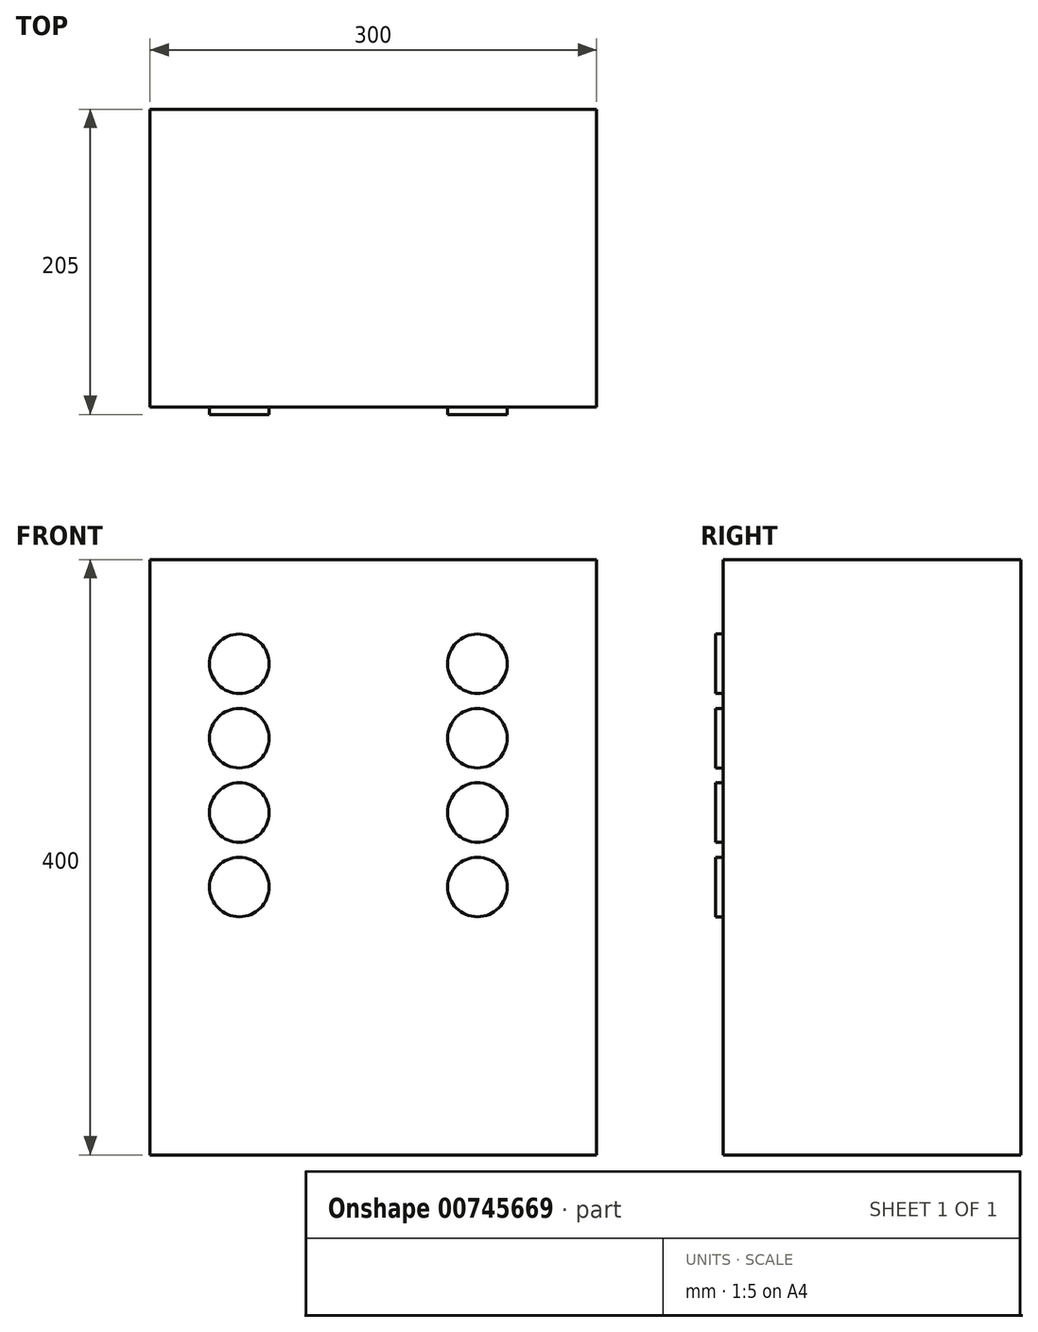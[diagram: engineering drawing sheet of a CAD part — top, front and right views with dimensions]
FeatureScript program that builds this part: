
annotation { "Feature Type Name" : "Feature", "Feature Type Description" : "" }
export const myFeature = defineFeature(function(context is Context, id is Id, definition is map)
    precondition{}
    {
        {
            var Q0;
            Q0=qCreatedBy(makeId("Front.planeOp"),FACE);
            var sketch = newSketch(context, id + "F0", { "sketchPlane" : qUnion([Q0])});
            skLineSegment(sketch, "E0.bottom", {"start": v(0, 0) * mm, "end": v(300, 0) * mm});
            skLineSegment(sketch, "E0.top", {"start": v(0, 400) * mm, "end": v(300, 400) * mm});
            skLineSegment(sketch, "E0.left", {"start": v(0, 0) * mm, "end": v(0, 400) * mm});
            skLineSegment(sketch, "E0.right", {"start": v(300, 0) * mm, "end": v(300, 400) * mm});
            skSolve(sketch);
        }
        {
            var Q0;
            Q0=makeQuery(id+"F0.imprint","IMPRINT",FACE,{"disambiguationData":[TD([[makeQuery(id+"F0.imprint","IMPRINT",EDGE,{"derivedFrom":sQuery(id+"F0.wireOp",EDGE,"E0.bottom")}),1.0]])]});
            extrude(context, id + "F1", {"entities" : qUnion([Q0]), "depth" : 200 * mm, "offsetDistance" : 25 * mm});
        }
        {
            var Q0;
            Q0=makeQuery(id+"F1.opExtrude","CAP_FACE",FACE,{"disambiguationData":[OSD([sQuery(id+"F0.wireOp",EDGE,"E0.bottom"),sQuery(id+"F0.wireOp",EDGE,"E0.top"),sQuery(id+"F0.wireOp",EDGE,"E0.left"),sQuery(id+"F0.wireOp",EDGE,"E0.right")])],"isStart":false});
            var sketch = newSketch(context, id + "F2", { "sketchPlane" : qUnion([Q0])});
            skCircle(sketch, "E1", {"center": v(60, 330) * mm, "radius": 20 * mm});
            skCircle(sketch, "E2.0.1.0", {"center": v(60, 280) * mm, "radius": 20 * mm});
            skCircle(sketch, "E2.0.2.0", {"center": v(60, 230) * mm, "radius": 20 * mm});
            skCircle(sketch, "E2.0.3.0", {"center": v(60, 180) * mm, "radius": 20 * mm});
            skCircle(sketch, "E2.1.0.0", {"center": v(220, 330) * mm, "radius": 20 * mm});
            skCircle(sketch, "E2.1.1.0", {"center": v(220, 280) * mm, "radius": 20 * mm});
            skCircle(sketch, "E2.1.2.0", {"center": v(220, 230) * mm, "radius": 20 * mm});
            skCircle(sketch, "E2.1.3.0", {"center": v(220, 180) * mm, "radius": 20 * mm});
            skLineSegment(sketch, "E2.direction1", {"start": v(60, 330) * mm, "end": v(220, 330) * mm, "construction": true});
            skLineSegment(sketch, "E2.direction2", {"start": v(60, 330) * mm, "end": v(60, 280) * mm, "construction": true});
            skSolve(sketch);
        }
        {
            var Q0;
            Q0=makeQuery(id+"F2.imprint","IMPRINT",FACE,{"disambiguationData":[TD([[makeQuery(id+"F2.imprint","IMPRINT",EDGE,{"derivedFrom":sQuery(id+"F2.wireOp",EDGE,"E2.0.1.0")}),1.0]])]});
            var Q1;
            Q1=makeQuery(id+"F2.imprint","IMPRINT",FACE,{"disambiguationData":[TD([[makeQuery(id+"F2.imprint","IMPRINT",EDGE,{"derivedFrom":sQuery(id+"F2.wireOp",EDGE,"E1")}),1.0]])]});
            var Q2;
            Q2=makeQuery(id+"F2.imprint","IMPRINT",FACE,{"disambiguationData":[TD([[makeQuery(id+"F2.imprint","IMPRINT",EDGE,{"derivedFrom":sQuery(id+"F2.wireOp",EDGE,"E2.0.2.0")}),1.0]])]});
            var Q3;
            Q3=makeQuery(id+"F2.imprint","IMPRINT",FACE,{"disambiguationData":[TD([[makeQuery(id+"F2.imprint","IMPRINT",EDGE,{"derivedFrom":sQuery(id+"F2.wireOp",EDGE,"E2.0.3.0")}),1.0]])]});
            var Q4;
            Q4=makeQuery(id+"F2.imprint","IMPRINT",FACE,{"disambiguationData":[TD([[makeQuery(id+"F2.imprint","IMPRINT",EDGE,{"derivedFrom":sQuery(id+"F2.wireOp",EDGE,"E2.1.0.0")}),1.0]])]});
            var Q5;
            Q5=makeQuery(id+"F2.imprint","IMPRINT",FACE,{"disambiguationData":[TD([[makeQuery(id+"F2.imprint","IMPRINT",EDGE,{"derivedFrom":sQuery(id+"F2.wireOp",EDGE,"E2.1.1.0")}),1.0]])]});
            var Q6;
            Q6=makeQuery(id+"F2.imprint","IMPRINT",FACE,{"disambiguationData":[TD([[makeQuery(id+"F2.imprint","IMPRINT",EDGE,{"derivedFrom":sQuery(id+"F2.wireOp",EDGE,"E2.1.2.0")}),1.0]])]});
            var Q7;
            Q7=makeQuery(id+"F2.imprint","IMPRINT",FACE,{"disambiguationData":[TD([[makeQuery(id+"F2.imprint","IMPRINT",EDGE,{"derivedFrom":sQuery(id+"F2.wireOp",EDGE,"E2.1.3.0")}),1.0]])]});
            extrude(context, id + "F3", {"entities" : qUnion([Q0, Q1, Q2, Q3, Q4, Q5, Q6, Q7]), "depth" : 5 * mm, "offsetDistance" : 25 * mm});
        }
    });
